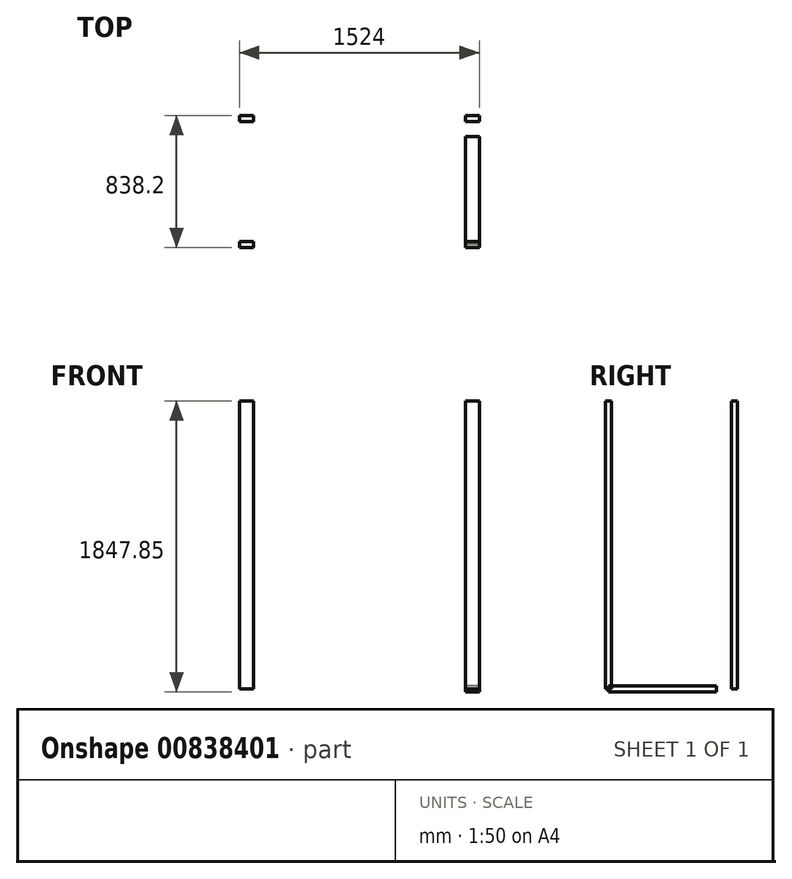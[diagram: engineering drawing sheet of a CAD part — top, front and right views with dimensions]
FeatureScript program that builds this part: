
annotation { "Feature Type Name" : "Feature", "Feature Type Description" : "" }
export const myFeature = defineFeature(function(context is Context, id is Id, definition is map)
    precondition{}
    {
        {
            var Q0;
            Q0=qCreatedBy(makeId("Top.planeOp"),FACE);
            var sketch = newSketch(context, id + "F0", { "sketchPlane" : qUnion([Q0])});
            skLineSegment(sketch, "E0.bottom", {"start": v(44.45, 19.05) * mm, "end": v(-44.45, 19.05) * mm});
            skLineSegment(sketch, "E0.top", {"start": v(44.45, -19.05) * mm, "end": v(-44.45, -19.05) * mm});
            skLineSegment(sketch, "E0.left", {"start": v(44.45, 19.05) * mm, "end": v(44.45, -19.05) * mm});
            skLineSegment(sketch, "E0.right", {"start": v(-44.45, 19.05) * mm, "end": v(-44.45, -19.05) * mm});
            skPoint(sketch, "E0.middle", {"position": v(0, 0) * mm});
            skSolve(sketch);
        }
        {
            var Q0;
            Q0=makeQuery(id+"F0.imprint","IMPRINT",FACE,{"disambiguationData":[TD([[makeQuery(id+"F0.imprint","IMPRINT",EDGE,{"derivedFrom":sQuery(id+"F0.wireOp",EDGE,"E0.bottom")}),1.0]])]});
            extrude(context, id + "F1", {"entities" : qUnion([Q0]), "depth" : 1828.8 * mm, "offsetDistance" : 25.4 * mm});
        }
        {
            var Q0;
            Q0=makeQuery(id+"F1.opExtrude","SWEPT_FACE",FACE,{"disambiguationData":[OSD([sQuery(id+"F0.wireOp",EDGE,"E0.bottom")])]});
            var sketch = newSketch(context, id + "F2", { "sketchPlane" : qUnion([Q0])});
            skSolve(sketch);
        }
        {
            var Q0;
            Q0=makeQuery(id+"F1.opExtrude","SWEPT_BODY",BODY,{"disambiguationData":[OSD([sQuery(id+"F0.wireOp",EDGE,"E0.bottom"),sQuery(id+"F0.wireOp",EDGE,"E0.top"),sQuery(id+"F0.wireOp",EDGE,"E0.left"),sQuery(id+"F0.wireOp",EDGE,"E0.right")])]});
            transform(context, id + "F3", {"entities" : qUnion([Q0]), "transformType" : TransformType.TRANSLATION_3D, "dx" : 0 * mm, "dy" : 800.1 * mm, "dz" : 0 * mm, "makeCopy" : true});
        }
        {
            var Q0;
            Q0=makeQuery(id+"F1.opExtrude","SWEPT_BODY",BODY,{"disambiguationData":[OSD([sQuery(id+"F0.wireOp",EDGE,"E0.bottom"),sQuery(id+"F0.wireOp",EDGE,"E0.top"),sQuery(id+"F0.wireOp",EDGE,"E0.left"),sQuery(id+"F0.wireOp",EDGE,"E0.right")])]});
            transform(context, id + "F4", {"entities" : qUnion([Q0]), "transformType" : TransformType.TRANSLATION_3D, "dx" : -1435.1 * mm, "dy" : 0 * mm, "dz" : 0 * mm, "makeCopy" : true});
        }
        {
            var Q0;
            Q0=makeQuery(id+"F3.opPattern","COPY",BODY,{"derivedFrom":makeQuery(id+"F1.opExtrude","SWEPT_BODY",BODY,{"disambiguationData":[OSD([sQuery(id+"F0.wireOp",EDGE,"E0.bottom"),sQuery(id+"F0.wireOp",EDGE,"E0.top"),sQuery(id+"F0.wireOp",EDGE,"E0.left"),sQuery(id+"F0.wireOp",EDGE,"E0.right")])]}),"instanceName":"1"});
            transform(context, id + "F5", {"entities" : qUnion([Q0]), "transformType" : TransformType.TRANSLATION_3D, "dx" : -1435.1 * mm, "dy" : 0 * mm, "dz" : 0 * mm, "makeCopy" : true});
        }
        {
            var Q0;
            Q0=qCreatedBy(makeId("Front.planeOp"),FACE);
            var sketch = newSketch(context, id + "F6", { "sketchPlane" : qUnion([Q0])});
            skLineSegment(sketch, "E1.bottom", {"start": v(44.45, 19.05) * mm, "end": v(-44.45, 19.05) * mm});
            skLineSegment(sketch, "E1.top", {"start": v(44.45, -19.05) * mm, "end": v(-44.45, -19.05) * mm});
            skLineSegment(sketch, "E1.left", {"start": v(44.45, 19.05) * mm, "end": v(44.45, -19.05) * mm});
            skLineSegment(sketch, "E1.right", {"start": v(-44.45, 19.05) * mm, "end": v(-44.45, -19.05) * mm});
            skPoint(sketch, "E1.middle", {"position": v(0, 0) * mm});
            skPoint(sketch, "E2.middle", {"position": v(44.45, 0) * mm});
            skPoint(sketch, "E2.cornerSnap0", {"position": v(44.45, 0) * mm});
            skSolve(sketch);
        }
        {
            var Q0;
            Q0 = qSketchRegion(id + "F2", true);
            var Q1;
            Q1 = qSketchRegion(id + "F6", true);
            extrude(context, id + "F7", {"entities" : qUnion([Q0, Q1]), "depth" : -685.8 * mm, "offsetDistance" : 25.4 * mm});
        }
    });
